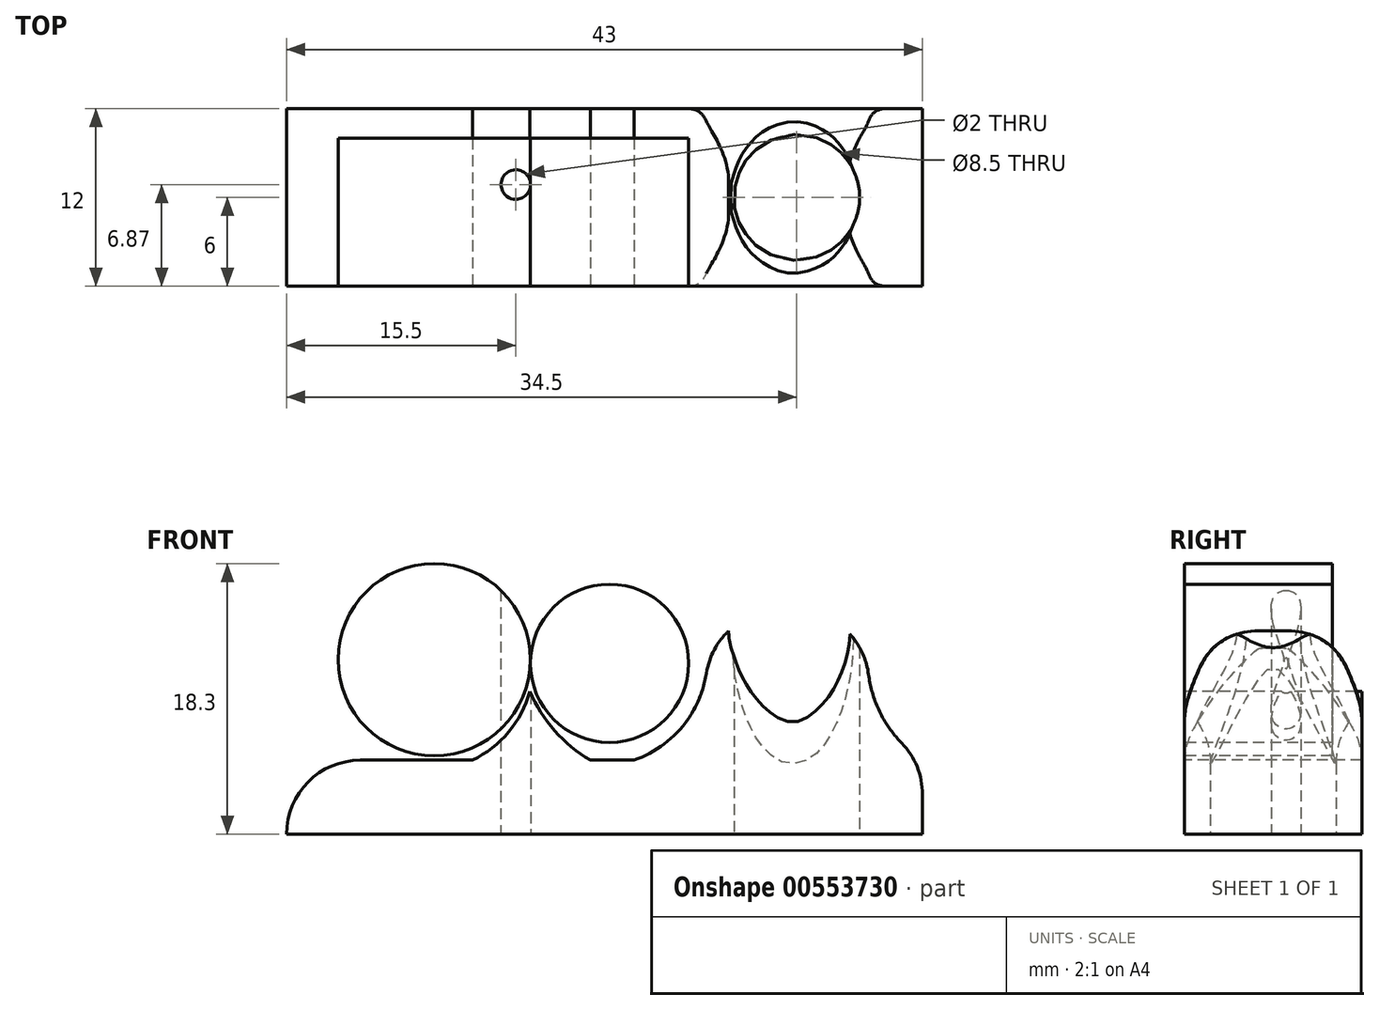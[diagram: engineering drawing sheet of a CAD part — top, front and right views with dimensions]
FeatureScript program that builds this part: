
annotation { "Feature Type Name" : "Feature", "Feature Type Description" : "" }
export const myFeature = defineFeature(function(context is Context, id is Id, definition is map)
    precondition{}
    {
        {
            var Q0;
            Q0=qCreatedBy(makeId("Top.planeOp"),FACE);
            var sketch = newSketch(context, id + "F0", { "sketchPlane" : qUnion([Q0])});
            skLineSegment(sketch, "E0.bottom", {"start": v(-21.5, -6) * mm, "end": v(21.5, -6) * mm});
            skLineSegment(sketch, "E0.top", {"start": v(-21.5, 6) * mm, "end": v(21.5, 6) * mm});
            skLineSegment(sketch, "E0.left", {"start": v(-21.5, -6) * mm, "end": v(-21.5, 6) * mm});
            skLineSegment(sketch, "E0.right", {"start": v(21.5, -6) * mm, "end": v(21.5, 6) * mm});
            skPoint(sketch, "E0.middle", {"position": v(0, 0) * mm});
            skCircle(sketch, "E1", {"center": v(-6, 0.87) * mm, "radius": 1 * mm});
            skCircle(sketch, "E2", {"center": v(13, 0) * mm, "radius": 4.25 * mm});
            skLineSegment(sketch, "E3", {"start": v(-5, 0.87) * mm, "end": v(-5, -18.43) * mm, "construction": true});
            skLineSegment(sketch, "E4", {"start": v(-7, 0.79) * mm, "end": v(-7, -18.4) * mm, "construction": true});
            skSolve(sketch);
        }
        {
            var Q0;
            Q0=makeQuery(id+"F0.imprint","IMPRINT",FACE,{"disambiguationData":[TD([[makeQuery(id+"F0.imprint","IMPRINT",EDGE,{"derivedFrom":sQuery(id+"F0.wireOp",EDGE,"E0.bottom")}),1.0]])]});
            extrude(context, id + "F1", {"entities" : qUnion([Q0]), "depth" : 5 * mm, "offsetDistance" : 25 * mm});
        }
        {
            var Q0;
            Q0=makeQuery(id+"F1.opExtrude","SWEPT_FACE",FACE,{"disambiguationData":[OSD([sQuery(id+"F0.wireOp",EDGE,"E0.bottom")])]});
            var sketch = newSketch(context, id + "F2", { "sketchPlane" : qUnion([Q0])});
            skCircle(sketch, "E5", {"center": v(0.34, 11.55) * mm, "radius": 5.35 * mm});
            skCircle(sketch, "E6", {"center": v(-11.5, 11.8) * mm, "radius": 6.5 * mm});
            skLineSegment(sketch, "E7", {"start": v(-7.01, 0) * mm, "end": v(-7.01, 29.7) * mm, "construction": true});
            skLineSegment(sketch, "E8", {"start": v(-5.01, 0) * mm, "end": v(-5.01, 27.45) * mm, "construction": true});
            skSolve(sketch);
        }
        {
            var Q0;
            Q0 = qSketchRegion(id + "F2", true);
            extrude(context, id + "F3", {"entities" : qUnion([Q0]), "oppositeDirection" : true, "depth" : 10 * mm, "offsetDistance" : 25 * mm});
        }
        {
            var Q0;
            Q0=makeQuery(id+"F1.opExtrude","SWEPT_FACE",FACE,{"disambiguationData":[OSD([sQuery(id+"F0.wireOp",EDGE,"E0.bottom")])]});
            var sketch = newSketch(context, id + "F4", { "sketchPlane" : qUnion([Q0])});
            skArc(sketch, "E9", {"start": v(-8.93, 5) * mm, "mid": v(-6.49, 6.9) * mm, "end": v(-5.05, 9.65) * mm});
            skArc(sketch, "E10", {"start": v(-5.05, 9.65) * mm, "mid": v(-3.37, 7) * mm, "end": v(-0.96, 5) * mm});
            skArc(sketch, "E11", {"start": v(1.99, 5) * mm, "mid": v(6.06, 8.45) * mm, "end": v(6.77, 13.74) * mm});
            skArc(sketch, "E12", {"start": v(18, 13.74) * mm, "mid": v(18.37, 8.82) * mm, "end": v(21.5, 5) * mm});
            skLineSegment(sketch, "E13", {"start": v(6.77, 13.74) * mm, "end": v(18, 13.74) * mm});
            skCircle(sketch, "E14", {"center": v(12.39, 13.74) * mm, "radius": 4 * mm});
            skSolve(sketch);
        }
        {
            var Q0;
            {var subQ0=sQuery(id+"F4.wireOp",EDGE,"E9");Q0=makeQuery(id+"F4.imprint","IMPRINT",FACE,{"disambiguationData":[TD([[makeQuery(id+"F4.imprint","IMPRINT",EDGE,{"derivedFrom":subQ0}),-1.0]])]});}
            var Q1;
            {var subQ4=sQuery(id+"F4.wireOp",EDGE,"E11");Q1=makeQuery(id+"F4.imprint","IMPRINT",FACE,{"disambiguationData":[TD([[makeQuery(id+"F4.imprint","IMPRINT",EDGE,{"derivedFrom":subQ4}),-1.0]])]});}
            extrude(context, id + "F5", {"entities" : qUnion([Q0, Q1]), "oppositeDirection" : true, "depth" : 12 * mm, "offsetDistance" : 25 * mm});
        }
        {
            var Q0;
            Q0=makeQuery(id+"F0.imprint","IMPRINT",FACE,{"disambiguationData":[TD([[makeQuery(id+"F0.imprint","IMPRINT",EDGE,{"derivedFrom":sQuery(id+"F0.wireOp",EDGE,"E1")}),1.0]])]});
            var Q1;
            Q1=makeQuery(id+"F0.imprint","IMPRINT",FACE,{"disambiguationData":[TD([[makeQuery(id+"F0.imprint","IMPRINT",EDGE,{"derivedFrom":sQuery(id+"F0.wireOp",EDGE,"E2")}),1.0]])]});
            extrude(context, id + "F6", {"entities" : qUnion([Q0, Q1]), "operationType" : NewBodyOperationType.REMOVE, "depth" : 25 * mm, "offsetDistance" : 25 * mm});
        }
        {
            var Q0;
            Q0=makeQuery(id+"F1.opExtrude","SWEPT_BODY",BODY,{"disambiguationData":[OSD([sQuery(id+"F0.wireOp",EDGE,"E0.bottom"),sQuery(id+"F0.wireOp",EDGE,"E0.top"),sQuery(id+"F0.wireOp",EDGE,"E0.left"),sQuery(id+"F0.wireOp",EDGE,"E0.right"),sQuery(id+"F0.wireOp",EDGE,"E1"),sQuery(id+"F0.wireOp",EDGE,"E2")])]});
            var Q1;
            Q1=makeQuery(id+"F5.opExtrude","SWEPT_BODY",BODY,{"disambiguationData":[OSD([sQuery(id+"F0.wireOp",EDGE,"E0.bottom"),sQuery(id+"F4.wireOp",EDGE,"E9"),sQuery(id+"F4.wireOp",EDGE,"E10")])]});
            var Q2;
            Q2=makeQuery(id+"F5.opExtrude","SWEPT_BODY",BODY,{"disambiguationData":[OSD([sQuery(id+"F0.wireOp",EDGE,"E0.bottom"),sQuery(id+"F4.wireOp",EDGE,"E11"),sQuery(id+"F4.wireOp",EDGE,"E12"),sQuery(id+"F4.wireOp",EDGE,"E13"),sQuery(id+"F4.wireOp",EDGE,"E14")])]});
            booleanBodies(context, id + "F7", {"operationType" : BooleanOperationType.UNION, "tools" : qUnion([Q0, Q1, Q2])});
        }
        {
            var Q0;
            Q0=makeQuery(id+"F1.opExtrude","CAP_EDGE",EDGE,{"disambiguationData":[OSD([sQuery(id+"F0.wireOp",EDGE,"E0.left")])],"isStart":false});
            var Q1;
            {var subQ0=sQuery(id+"F0.wireOp",EDGE,"E0.right");Q1=makeQuery(id+"F7.opBoolean","MERGE",EDGE,{"derivedFrom":[makeQuery(id+"F1.opExtrude","CAP_EDGE",EDGE,{"disambiguationData":[OSD([subQ0])],"isStart":false}),makeQuery(id+"F5.opExtrude","SWEPT_EDGE",EDGE,{"disambiguationData":[OSD([sQuery(id+"F0.wireOp",EDGE,"E0.bottom"),subQ0,sQuery(id+"F4.wireOp",EDGE,"E12")])]})]});}
            var Q2;
            Q2=makeQuery(id+"F5.opExtrude","SWEPT_EDGE",EDGE,{"disambiguationData":[OSD([sQuery(id+"F4.wireOp",EDGE,"E12"),sQuery(id+"F4.wireOp",EDGE,"E13")])]});
            var Q3;
            Q3=makeQuery(id+"F5.opExtrude","SWEPT_EDGE",EDGE,{"disambiguationData":[OSD([sQuery(id+"F4.wireOp",EDGE,"E11"),sQuery(id+"F4.wireOp",EDGE,"E13")])]});
            var Q4;
            Q4=makeQuery(id+"F5.opExtrude","SWEPT_EDGE",EDGE,{"disambiguationData":[OSD([sQuery(id+"F0.wireOp",EDGE,"E0.bottom"),sQuery(id+"F4.wireOp",EDGE,"E11")])]});
            var Q5;
            Q5=makeQuery(id+"F5.opExtrude","SWEPT_EDGE",EDGE,{"disambiguationData":[OSD([sQuery(id+"F0.wireOp",EDGE,"E0.bottom"),sQuery(id+"F4.wireOp",EDGE,"E10")])]});
            var Q6;
            Q6=makeQuery(id+"F5.opExtrude","SWEPT_EDGE",EDGE,{"disambiguationData":[OSD([sQuery(id+"F0.wireOp",EDGE,"E0.bottom"),sQuery(id+"F4.wireOp",EDGE,"E9")])]});
            fillet(context, id + "F8", {"entities" : qUnion([Q0, Q1, Q2, Q3, Q4, Q5, Q6]), "radius" : 5 * mm, "tangentPropagation" : true, "allowEdgeOverflow" : false});
        }
        {
            var Q0;
            Q0=makeQuery(id+"F5.opExtrude","CAP_EDGE",EDGE,{"disambiguationData":[OSD([sQuery(id+"F4.wireOp",EDGE,"E14")])],"isStart":true});
            var Q1;
            Q1=makeQuery(id+"F5.opExtrude","CAP_EDGE",EDGE,{"disambiguationData":[OSD([sQuery(id+"F4.wireOp",EDGE,"E14")])],"isStart":false});
            fillet(context, id + "F9", {"entities" : qUnion([Q0, Q1]), "radius" : 5 * mm, "tangentPropagation" : true, "allowEdgeOverflow" : false});
        }
        {
            var Q0;
            {var subQ0=sQuery(id+"F0.wireOp",EDGE,"E2");Q0=makeQuery(id+"F9.opFillet","BLEND_EDGE",EDGE,{"blendedFrom":[makeQuery(id+"F5.opExtrude","CAP_EDGE",EDGE,{"disambiguationData":[OSD([sQuery(id+"F4.wireOp",EDGE,"E14")])],"isStart":false}),makeQuery(id+"F7.opBoolean","MERGE",FACE,{"derivedFrom":[makeQuery(id+"F1.opExtrude","SWEPT_FACE",FACE,{"disambiguationData":[OSD([subQ0])]}),makeQuery(id+"F6.boolean.opBoolean","COPY",FACE,{"derivedFrom":makeQuery(id+"F6.opExtrude","SWEPT_FACE",FACE,{"disambiguationData":[OSD([subQ0])]})})]})],"blendedInto":[makeQuery(id+"F7.opBoolean","MERGE",FACE,{"derivedFrom":[makeQuery(id+"F1.opExtrude","SWEPT_FACE",FACE,{"disambiguationData":[OSD([subQ0])]}),makeQuery(id+"F6.boolean.opBoolean","COPY",FACE,{"derivedFrom":makeQuery(id+"F6.opExtrude","SWEPT_FACE",FACE,{"disambiguationData":[OSD([subQ0])]})})]})]});}
            fillet(context, id + "F10", {"entities" : qUnion([Q0]), "radius" : 5 * mm, "tangentPropagation" : true, "allowEdgeOverflow" : false});
        }
    });
